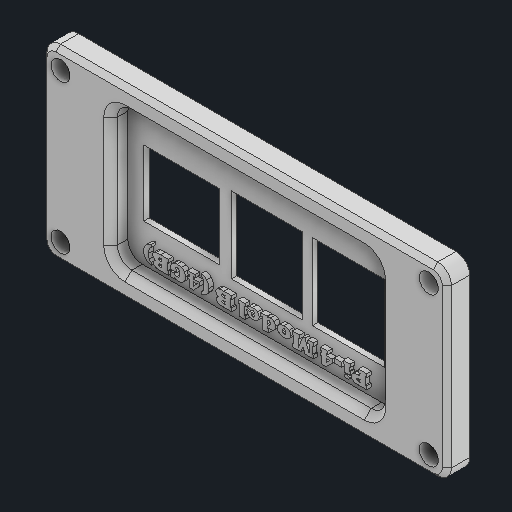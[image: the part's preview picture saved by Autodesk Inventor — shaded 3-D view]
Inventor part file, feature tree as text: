
AUTODESK INVENTOR PART (.ipt)
format: ipt  version: 2024 (Build 280153000, 153)  size: 640,000 bytes
history: native  units: in
note: dims shown in document units (in); Inventor stores cm internally (conversion verified against a paired STEP export)
features: reference x22, extrude x4, sketch x4, other x3, chamfer x2, projected_geometry x2, fillet x1
ambient origin geometry x8: Origin, YZ Plane, XZ Plane, XY Plane, X Axis, Y Axis, Z Axis, Center Point
bodies: Solid1 (feature_tree)
feature tree (38):
  extrude  "Extrusion1"  Depth=0.0472in TaperAngle=0.0deg
  extrude  "Extrusion2"  Depth=0.1969in
  fillet  "Fillet1"  Radius=0.1969in
  extrude  "Extrusion3"  Depth=0.1969in TaperAngle=0.0deg
  chamfer  "Chamfer1"  Distance=0.0591in Angle=45.0deg
  chamfer  "Chamfer2"  Distance=0.1181in
  extrude  "Extrusion4"  Depth=0.1181in
  sketch  "Sketch1"  dims[d0=0.0591in d1=0.0472in d2=0.0in]
  reference  "Reference1"
  reference  "Reference2"
  reference  "Reference3"
  reference  "Reference4"
  reference  "Reference5"
  reference  "Reference6"
  reference  "Reference7"
  reference  "Reference8"
  reference  "Reference9"
  reference  "Reference10"
  reference  "Reference11"
  reference  "Reference12"
  reference  "Reference13"
  reference  "Reference14"
  reference  "Reference15"
  reference  "Reference16"
  reference  "Reference17"
  reference  "Reference18"
  reference  "Reference19"
  reference  "Reference20"
  sketch  "Sketch2"  dims[d3=0.0394in d4=0.0in d5=0.125in d6=0.1969in]
  sketch  "Sketch3"  dims[d7=0.5906in d8=0.1969in d9=0.0in]
  projected_geometry  "Projected Loop1"
  sketch  "Sketch4"  dims[d10=0.5906in d11=0.0591in d12=0.125in d13=45.0deg d14=0.1181in d15=0.1654in d16=0.1654in d17=0.1654in d18=0.1654in d19=0.1575in d20=0.1575in d21=0.1575in d22=0.1575in d23=0.1575in d24=0.1575in d25=0.1575in d26=0.1575in d27=0.0394in d28=0.125in d29=45.0deg d31=0.126in d32=0.126in d33=0.6693in d34=0.4724in d35=0.1181in d36=0.0in]
  projected_geometry  "Projected Loop2"
  reference  "Reference21"
  reference  "Reference22"
  other  "<userpath>\Desktop\SeniorDesign\Head_V3\RaspberryPi_Encloser.iam"
  other  "RaspberryPi_Encloser.iam"
  other  "RaspberryPi_baseplate:1"
